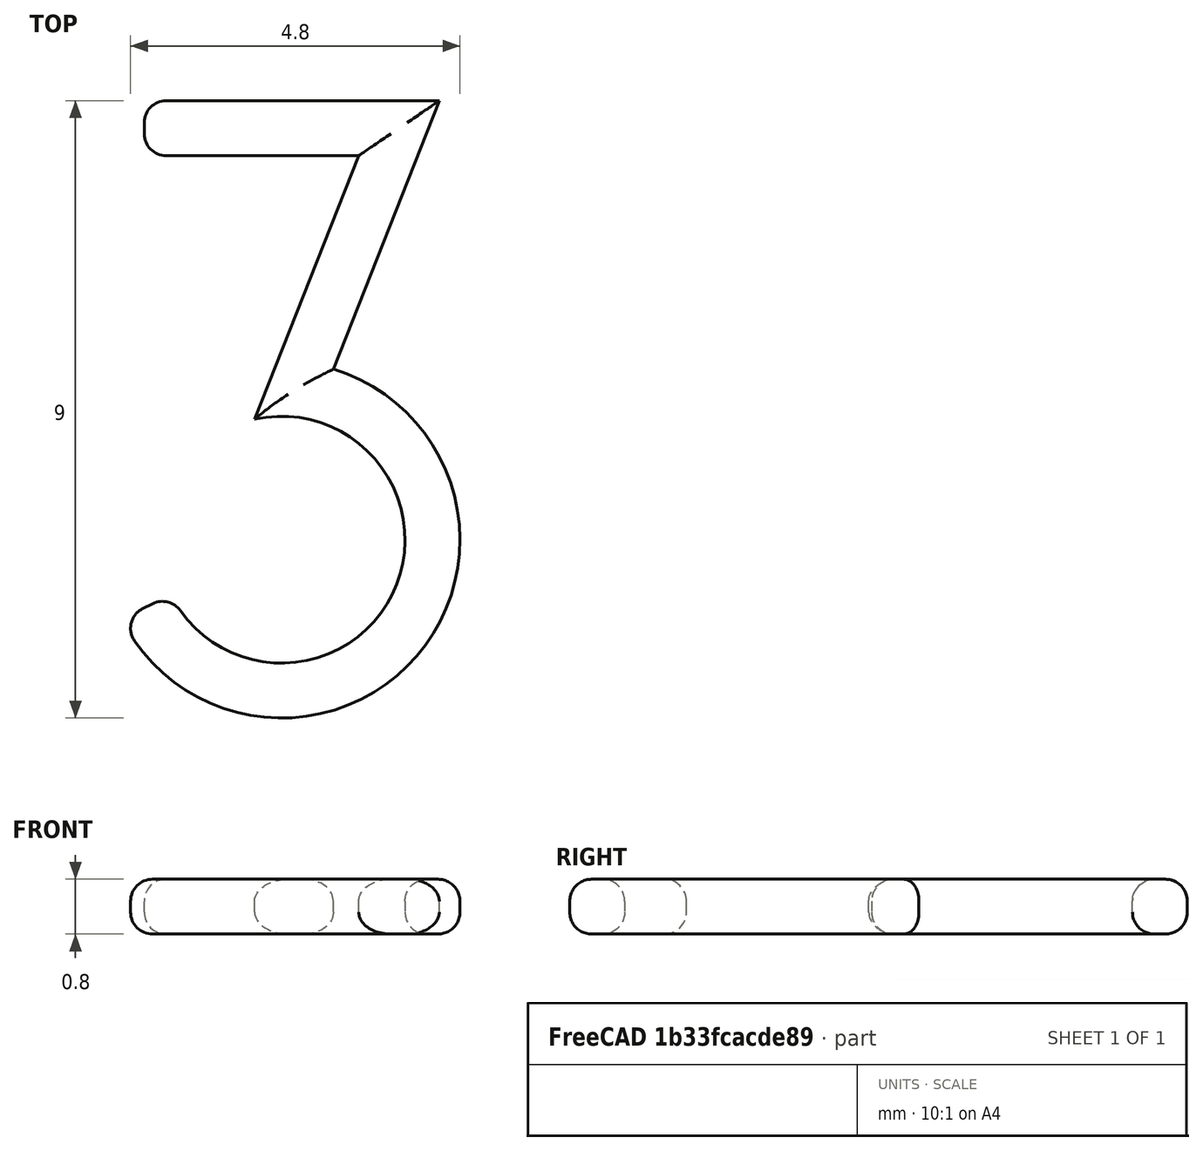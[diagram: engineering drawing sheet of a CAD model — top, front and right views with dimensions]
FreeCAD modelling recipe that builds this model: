
FCSTD DOCUMENT  (FreeCAD 0.16R6712 (Git))
Label: 3
License: All rights reserved
LicenseURL: http://en.wikipedia.org/wiki/All_rights_reserved
objects: Sketcher::SketchObject×1, PartDesign::Pad×1, PartDesign::Fillet×1, Mesh::Feature×1
note: 4 computed .brp shape members not serialized (recipe doc carries the construction recipe); baked Part::Feature solids carry a one-line shape summary decoded from their .brp

FEATURE [Sketcher::SketchObject] Sketch
  sketch-geometry (8):
    g0: ArcOfCircle CenterX=0 CenterY=2.6 CenterZ=0 NormalX=0 NormalY=0 NormalZ=1 Radius=1.8 StartAngle=3.60289 EndAngle=8.07305
    g1: LineSegment StartX=-1.61186 StartY=1.7988 StartZ=0 EndX=-2.32824 EndY=1.44271 EndZ=0
    g2: ArcOfCircle CenterX=0 CenterY=2.6 CenterZ=0 NormalX=0 NormalY=0 NormalZ=1 Radius=2.6 StartAngle=3.60289 EndAngle=7.5586
    g3: LineSegment StartX=-2 StartY=9 StartZ=0 EndX=2.3 EndY=9 EndZ=0
    g4: LineSegment StartX=-2 StartY=9 StartZ=0 EndX=-2 EndY=8.2 EndZ=0
    g5: LineSegment StartX=-2 StartY=8.2 StartZ=0 EndX=1.12451 EndY=8.2 EndZ=0
    g6: LineSegment StartX=1.12451 StartY=8.2 StartZ=0 EndX=-0.391169 EndY=4.35698 EndZ=0
    g7: LineSegment StartX=2.3 StartY=9 StartZ=0 EndX=0.756876 EndY=5.0874 EndZ=0
  constraints (23):
    c: Coincident(g1,g0)
    c: Perpendicular(g0,g1)
    c: Distance(g0,g1) = 0.8
    c: PointOnObject(g0,g-2)
    c: Coincident(g2,g0)
    c: Coincident(g2,g1)
    c: Tangent(g-1,g2)
    c: Horizontal(g3)
    c: Coincident(g4,g3)
    c: Vertical(g4)
    c: Horizontal(g5)
    c: Distance(g4,g3) = 0.8
    c: DistanceY(g-1,g3) = 9
    c: Coincident(g5,g4)
    c: Coincident(g6,g5)
    c: DistanceX(g-2,g3) = -2
    c: DistanceX(g-2,g3) = 2.3
    c: Coincident(g7,g3)
    c: Coincident(g2,g7)
    c: Coincident(g0,g6)
    c: Distance(g2,g6) = 0.8
    c: Radius(g2) = 2.6
    c: Parallel(g6,g7)
FEATURE [PartDesign::Pad] Pad
  Length = 0.8
  Length2 = 100
  Midplane = true
  Sketch = -> Sketch
  Type = 0
FEATURE [PartDesign::Fillet] Fillet
  Base = -> Pad [Edge1,Edge20,Edge23,Edge24,Edge4,Edge7,Edge10,Edge13,Edge16,Edge19,Edge22,Edge11,Edge8,Edge12,Edge3,Edge6,Edge9,Edge15,Edge18,Edge21]
  Radius = 0.32
FEATURE [Mesh::Feature] Mesh  label="Fillet (Meshed)"
